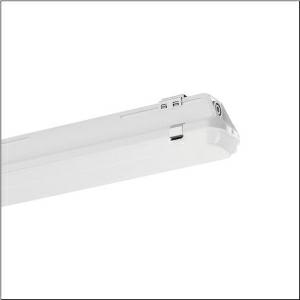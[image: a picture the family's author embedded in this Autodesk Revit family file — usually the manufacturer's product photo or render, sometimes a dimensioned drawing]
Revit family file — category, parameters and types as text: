
# Revit family: monsun_r__21_emergency_51fb107p437b3g_111f
name_source: partatom
category: Lighting Fixtures
units: mm (PartAtom-declared; Revit-internal decimal feet)

## family parameters
Cut with Voids When Loaded = No
Host = Face
Light Source = No
Part Type = Normal
Room Calculation Point = No
Round Connector Dimension = Use Diameter
Shared = No

## types (1)
- Monsun® 21 emergency (1 x LED, 3860 lm, 26.9 W, 4000K)
    Apparent Load = 27 VA
    CIE Flux Codes = 47 77 93 94 100
    Color Rendering = 80
    Color Temperature = 4000K
    Default Elevation = 1800 mm
    Description = Monsun® 21 emergency, damp-proof luminaire, chain hanger, primary optical cover: enclosure, of PMMA, light emission: direct distribution, primary light characteristic: symmetric, installation type: vertical mounting, horizontal mounting, surface-mounted, suspended mounting, LED, rated luminous flux: 3.860lm, luminous efficacy: 144lm/W, light colour: 840, colour temperature: 4000K, control gear: ECG, with terminal, 4-pole, max. 2.5mm², mains connection: 220..240V, AC, 50/60Hz, rated input power: 27W, control gear: single battery element, battery: NiCd, 4,5Ah, mains connection: 230V, housing, of glass-fibre reinforced polyester, uncoated, bright grey, length: 1.590mm, width: 90mm, height: 88mm, clip for enclosure, of stainless steel (V2A), ceiling mounting element, of stainless steel (V2A), chain hanger, of stainless steel (V2A), protection rating (complete): IP66, insulation class (complete): insulation class I (protective earthing), certification: CE, UKCA, protection symbol: D, impact resistance: IK04, permissible operating ambient temperature: +5..+25°C, standard: EN 60598-2-1, EN 50419, EN 60598-2-22, corresponds to IFS (International Featured Standards) requirements for safety and quality in the food industry, for indoor or canopied outdoor use, no direct snow, no direct sun, no direct rain, packaging unit: 1 piece
    Height = 89 mm
    Lamp = 1 x LED
    Lamp Light Flux = 3860 lm
    Lamp Power = 26.9 W
    Lamp count = 1
    Length = 1590 mm
    Luminous efficacy = 143 lm/W
    Manufacturer = Siteco
    ModVariant = No
    Model = 51FB107P437B3G
    Mounting Place = Ceiling
    Mounting Type = Pendant
    Number of Poles = 1
    OnlyDefault = Yes
    Power Factor = 1
    Product Name = Monsun® 21 emergency
    Product group = damp-proof luminaire | ceiling pendant
    ProductGroupID = 908
    Protection Class = Protection class I
    Protection Degree = IP 66
    RLX_Detail_Level = 1
    RlxData = <blob elided: 88829 chars, md5=95b78631>
    Socket = socket
    Standby Power = 0 W
    System Light Flux = 3860 lm
    System Power = 27 W
    Type Comments = Product without accessories
    Type Image = l_1006717.jpg
    URL = http://relux.com
    VarID = ---
    Voltage = 0 V
    Weight = 0.00 kg
    Width = 90 mm

## geometry (parser evidence)
native form markers: Blend x4, Sweep x12
no freeform markers — native parametric forms only
